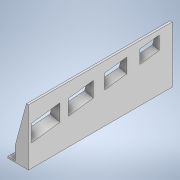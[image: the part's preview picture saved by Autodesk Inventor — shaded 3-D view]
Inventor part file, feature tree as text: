
AUTODESK INVENTOR PART (.ipt)
format: ipt  version: 2020 (Build 240168000, 168)  size: 275,456 bytes
history: native  units: mm
features: other x6, sketch x6, extrude x3, hole x2
ambient origin geometry x8: Origin, YZ Plane, XZ Plane, XY Plane, X Axis, Y Axis, Z Axis, Center Point
bodies: Body1 (feature_tree)
feature tree (17):
  other  "Твердое тело1"
  extrude  "Выдавливание1"  Depth=17.5mm
  sketch  "Эскиз2"
  other  "РабПлоскость1"
  other  "Разделение1"
  extrude  "Выдавливание2"  Depth=191.0mm
  extrude  "Выдавливание5"  Depth=75.0mm TaperAngle=0.0deg
  hole  "Отверстие1"  [1 undecoded]
  hole  "Отверстие2"  [1 undecoded]
  sketch  "Эскиз1"
  sketch  "Эскиз3"
  sketch  "Эскиз4"
  sketch  "Эскиз5"
  sketch  "Эскиз6"
  other  "Проецирование ребер1"
  other  "Проецирование ребер3"
  other  "Проецирование ребер4"
note: 2 required parameter values undecoded (feature->parameter linkage not recoverable at this tier; creation-order binding heuristic only, values carry confidence <= 0.55)
